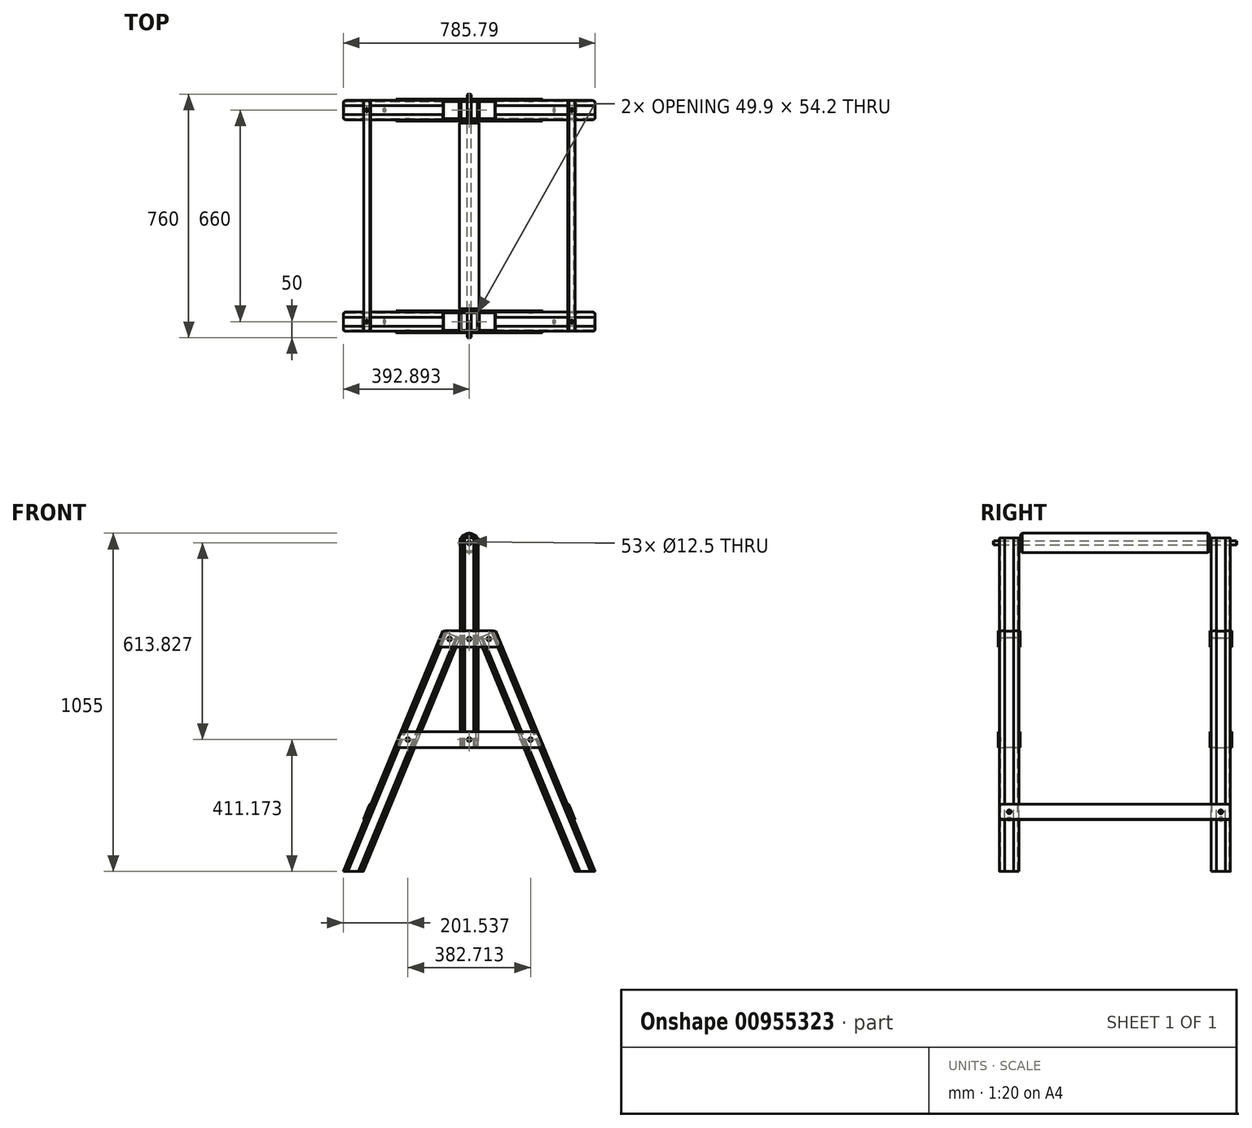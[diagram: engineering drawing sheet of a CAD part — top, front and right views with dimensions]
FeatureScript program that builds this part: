
annotation { "Feature Type Name" : "Feature", "Feature Type Description" : "" }
export const myFeature = defineFeature(function(context is Context, id is Id, definition is map)
    precondition{}
    {
        {
            var Q0;
            Q0=qCreatedBy(makeId("Front.planeOp"),FACE);
            var sketch = newSketch(context, id + "F0", { "sketchPlane" : qUnion([Q0])});
            skLineSegment(sketch, "E0", {"start": v(0, 0) * mm, "end": v(-310.74, 750.2) * mm});
            skLineSegment(sketch, "E1", {"start": v(-310.74, 750.2) * mm, "end": v(-364.05, 728.1) * mm});
            skLineSegment(sketch, "E2", {"start": v(-364.05, 728.1) * mm, "end": v(-62.45, 0) * mm});
            skLineSegment(sketch, "E3", {"start": v(-62.45, 0) * mm, "end": v(0, 0) * mm});
            skLineSegment(sketch, "E4", {"start": v(-337.4, 739.15) * mm, "end": v(-31.23, 0) * mm, "construction": true});
            skCircle(sketch, "E5", {"center": v(-331.65, 725.3) * mm, "radius": 6.25 * mm});
            skCircle(sketch, "E6", {"center": v(-201.54, 411.17) * mm, "radius": 6.25 * mm});
            skSolve(sketch);
        }
        {
            var Q0;
            Q0 = qSketchRegion(id + "F0", true);
            extrude(context, id + "F1", {"entities" : qUnion([Q0]), "depth" : 60 * mm, "offsetDistance" : 25 * mm});
        }
        {
            var Q0;
            Q0=makeQuery(id+"F1.opExtrude","CAP_EDGE",EDGE,{"disambiguationData":[OSD([sQuery(id+"F0.wireOp",EDGE,"E0")])],"isStart":false});
            var Q1;
            Q1=makeQuery(id+"F1.opExtrude","CAP_EDGE",EDGE,{"disambiguationData":[OSD([sQuery(id+"F0.wireOp",EDGE,"E2")])],"isStart":false});
            var Q2;
            Q2=makeQuery(id+"F1.opExtrude","CAP_EDGE",EDGE,{"disambiguationData":[OSD([sQuery(id+"F0.wireOp",EDGE,"E0")])],"isStart":true});
            var Q3;
            Q3=makeQuery(id+"F1.opExtrude","CAP_EDGE",EDGE,{"disambiguationData":[OSD([sQuery(id+"F0.wireOp",EDGE,"E2")])],"isStart":true});
            fillet(context, id + "F2", {"entities" : qUnion([Q0, Q1, Q2, Q3]), "radius" : 7.5 * mm, "tangentPropagation" : true, "allowEdgeOverflow" : false});
        }
        {
            var Q0;
            Q0=makeQuery(id+"F1.opExtrude","SWEPT_FACE",FACE,{"disambiguationData":[OSD([sQuery(id+"F0.wireOp",EDGE,"E1")])]});
            var sketch = newSketch(context, id + "F3", { "sketchPlane" : qUnion([Q0])});
            skLineSegment(sketch, "E7", {"start": v(-50.2, -60) * mm, "end": v(-49.2, -59) * mm});
            skLineSegment(sketch, "E8", {"start": v(-49.2, -59) * mm, "end": v(-48.2, -60) * mm});
            skLineSegment(sketch, "E9", {"start": v(-48.2, -60) * mm, "end": v(-47.2, -59) * mm});
            skLineSegment(sketch, "E10", {"start": v(-47.2, -59) * mm, "end": v(-46.2, -60) * mm});
            skLineSegment(sketch, "E11", {"start": v(-46.2, -60) * mm, "end": v(-45.2, -59) * mm});
            skLineSegment(sketch, "E12", {"start": v(-45.2, -59) * mm, "end": v(-44.2, -60) * mm});
            skLineSegment(sketch, "E13", {"start": v(-28.85, -60) * mm, "end": v(-28.85, -30) * mm, "construction": true});
            skPoint(sketch, "E13.endSnap0", {"position": v(-57.7, -30) * mm});
            skLineSegment(sketch, "E14", {"start": v(-28.85, -30) * mm, "end": v(-57.7, -30) * mm, "construction": true});
            skLineSegment(sketch, "E15", {"start": v(-57.4, -44) * mm, "end": v(-57.7, -44) * mm});
            skLineSegment(sketch, "E16", {"start": v(-57.4, -44) * mm, "end": v(-57.4, -30) * mm});
            skArc(sketch, "E17.0", {"start": v(-54.8, -52.5) * mm, "mid": v(-53.45, -55.75) * mm, "end": v(-50.2, -57.1) * mm});
            skLineSegment(sketch, "E18", {"start": v(-54.8, -52.5) * mm, "end": v(-54.8, -30) * mm});
            skLineSegment(sketch, "E19", {"start": v(-50.2, -57.1) * mm, "end": v(-28.85, -57.1) * mm});
            skLineSegment(sketch, "E20.MirrorCS", {"start": v(-0.3, -44) * mm, "end": v(0, -44) * mm});
            skLineSegment(sketch, "E21.MirrorCS", {"start": v(-7.5, -60) * mm, "end": v(-8.5, -59) * mm});
            skLineSegment(sketch, "E22.MirrorCS", {"start": v(-11.5, -60) * mm, "end": v(-12.5, -59) * mm});
            skLineSegment(sketch, "E23.MirrorCS", {"start": v(-9.5, -60) * mm, "end": v(-10.5, -59) * mm});
            skLineSegment(sketch, "E24.MirrorCS", {"start": v(-12.5, -59) * mm, "end": v(-13.5, -60) * mm});
            skLineSegment(sketch, "E25.MirrorCS", {"start": v(-10.5, -59) * mm, "end": v(-11.5, -60) * mm});
            skLineSegment(sketch, "E26.MirrorCS", {"start": v(-8.5, -59) * mm, "end": v(-9.5, -60) * mm});
            skArc(sketch, "E27.MirrorCS", {"start": v(-2.9, -52.5) * mm, "mid": v(-4.25, -55.75) * mm, "end": v(-7.5, -57.1) * mm});
            skLineSegment(sketch, "E28.MirrorCS", {"start": v(-0.3, -44) * mm, "end": v(-0.3, -30) * mm});
            skLineSegment(sketch, "E29.MirrorCS", {"start": v(-7.5, -57.1) * mm, "end": v(-28.85, -57.1) * mm});
            skLineSegment(sketch, "E30.MirrorCS", {"start": v(-2.9, -52.5) * mm, "end": v(-2.9, -30) * mm});
            skLineSegment(sketch, "E31.MirrorCS", {"start": v(-50.2, 0) * mm, "end": v(-49.2, -1) * mm});
            skLineSegment(sketch, "E32.MirrorCS", {"start": v(-48.2, 0) * mm, "end": v(-47.2, -1) * mm});
            skLineSegment(sketch, "E33.MirrorCS", {"start": v(-49.2, -1) * mm, "end": v(-48.2, 0) * mm});
            skLineSegment(sketch, "E34.MirrorCS", {"start": v(-46.2, 0) * mm, "end": v(-45.2, -1) * mm});
            skLineSegment(sketch, "E35.MirrorCS", {"start": v(-47.2, -1) * mm, "end": v(-46.2, 0) * mm});
            skLineSegment(sketch, "E36.MirrorCS", {"start": v(-57.4, -16) * mm, "end": v(-57.7, -16) * mm});
            skLineSegment(sketch, "E37.MirrorCS", {"start": v(-45.2, -1) * mm, "end": v(-44.2, 0) * mm});
            skArc(sketch, "E38.MirrorCS", {"start": v(-54.8, -7.5) * mm, "mid": v(-53.45, -4.25) * mm, "end": v(-50.2, -2.9) * mm});
            skLineSegment(sketch, "E39.MirrorCS", {"start": v(-50.2, -2.9) * mm, "end": v(-28.85, -2.9) * mm});
            skLineSegment(sketch, "E40.MirrorCS", {"start": v(-54.8, -7.5) * mm, "end": v(-54.8, -30) * mm});
            skLineSegment(sketch, "E41.MirrorCS", {"start": v(-57.4, -16) * mm, "end": v(-57.4, -30) * mm});
            skLineSegment(sketch, "E42.MirrorCS", {"start": v(-9.5, 0) * mm, "end": v(-10.5, -1) * mm});
            skLineSegment(sketch, "E43.MirrorCS", {"start": v(-12.5, -1) * mm, "end": v(-13.5, 0) * mm});
            skLineSegment(sketch, "E44.MirrorCS", {"start": v(-10.5, -1) * mm, "end": v(-11.5, 0) * mm});
            skLineSegment(sketch, "E45.MirrorCS", {"start": v(-0.3, -16) * mm, "end": v(0, -16) * mm});
            skLineSegment(sketch, "E46.MirrorCS", {"start": v(-11.5, 0) * mm, "end": v(-12.5, -1) * mm});
            skLineSegment(sketch, "E47.MirrorCS", {"start": v(-7.5, 0) * mm, "end": v(-8.5, -1) * mm});
            skLineSegment(sketch, "E48.MirrorCS", {"start": v(-8.5, -1) * mm, "end": v(-9.5, 0) * mm});
            skLineSegment(sketch, "E49.MirrorCS", {"start": v(-2.9, -7.5) * mm, "end": v(-2.9, -30) * mm});
            skLineSegment(sketch, "E50.MirrorCS", {"start": v(-7.5, -2.9) * mm, "end": v(-28.85, -2.9) * mm});
            skArc(sketch, "E51.MirrorCS", {"start": v(-2.9, -7.5) * mm, "mid": v(-4.25, -4.25) * mm, "end": v(-7.5, -2.9) * mm});
            skLineSegment(sketch, "E52.MirrorCS", {"start": v(-0.3, -16) * mm, "end": v(-0.3, -30) * mm});
            skSolve(sketch);
        }
        {
            var Q0;
            Q0=makeQuery(id+"F3.imprint","IMPRINT",FACE,{"disambiguationData":[TD([[makeQuery(id+"F3.imprint","IMPRINT",EDGE,{"derivedFrom":sQuery(id+"F3.wireOp",EDGE,"E17.0")}),1.0]])]});
            var Q1;
            {var subQ0=sQuery(id+"F3.wireOp",EDGE,"E34.MirrorCS");Q1=makeQuery(id+"F3.imprint","IMPRINT",FACE,{"disambiguationData":[TD([[makeQuery(id+"F3.imprint","IMPRINT",EDGE,{"derivedFrom":subQ0}),1.0]])]});}
            var Q2;
            {var subQ0=sQuery(id+"F3.wireOp",EDGE,"E32.MirrorCS");Q2=makeQuery(id+"F3.imprint","IMPRINT",FACE,{"disambiguationData":[TD([[makeQuery(id+"F3.imprint","IMPRINT",EDGE,{"derivedFrom":subQ0}),1.0]])]});}
            var Q3;
            {var subQ0=sQuery(id+"F3.wireOp",EDGE,"E31.MirrorCS");Q3=makeQuery(id+"F3.imprint","IMPRINT",FACE,{"disambiguationData":[TD([[makeQuery(id+"F3.imprint","IMPRINT",EDGE,{"derivedFrom":subQ0}),1.0]])]});}
            var Q4;
            {var subQ1=sQuery(id+"F3.wireOp",EDGE,"E15");Q4=makeQuery(id+"F3.imprint","IMPRINT",FACE,{"disambiguationData":[TD([[makeQuery(id+"F3.imprint","IMPRINT",EDGE,{"derivedFrom":subQ1}),-1.0]])]});}
            var Q5;
            {var subQ0=sQuery(id+"F3.wireOp",EDGE,"E7");Q5=makeQuery(id+"F3.imprint","IMPRINT",FACE,{"disambiguationData":[TD([[makeQuery(id+"F3.imprint","IMPRINT",EDGE,{"derivedFrom":subQ0}),-1.0]])]});}
            var Q6;
            {var subQ0=sQuery(id+"F3.wireOp",EDGE,"E9");Q6=makeQuery(id+"F3.imprint","IMPRINT",FACE,{"disambiguationData":[TD([[makeQuery(id+"F3.imprint","IMPRINT",EDGE,{"derivedFrom":subQ0}),-1.0]])]});}
            var Q7;
            {var subQ0=sQuery(id+"F3.wireOp",EDGE,"E11");Q7=makeQuery(id+"F3.imprint","IMPRINT",FACE,{"disambiguationData":[TD([[makeQuery(id+"F3.imprint","IMPRINT",EDGE,{"derivedFrom":subQ0}),-1.0]])]});}
            var Q8;
            {var subQ0=sQuery(id+"F3.wireOp",EDGE,"E21.MirrorCS");Q8=makeQuery(id+"F3.imprint","IMPRINT",FACE,{"disambiguationData":[TD([[makeQuery(id+"F3.imprint","IMPRINT",EDGE,{"derivedFrom":subQ0}),1.0]])]});}
            var Q9;
            {var subQ0=sQuery(id+"F3.wireOp",EDGE,"E23.MirrorCS");Q9=makeQuery(id+"F3.imprint","IMPRINT",FACE,{"disambiguationData":[TD([[makeQuery(id+"F3.imprint","IMPRINT",EDGE,{"derivedFrom":subQ0}),1.0]])]});}
            var Q10;
            {var subQ0=sQuery(id+"F3.wireOp",EDGE,"E22.MirrorCS");Q10=makeQuery(id+"F3.imprint","IMPRINT",FACE,{"disambiguationData":[TD([[makeQuery(id+"F3.imprint","IMPRINT",EDGE,{"derivedFrom":subQ0}),1.0]])]});}
            var Q11;
            {var subQ1=sQuery(id+"F3.wireOp",EDGE,"E20.MirrorCS");Q11=makeQuery(id+"F3.imprint","IMPRINT",FACE,{"disambiguationData":[TD([[makeQuery(id+"F3.imprint","IMPRINT",EDGE,{"derivedFrom":subQ1}),1.0]])]});}
            var Q12;
            {var subQ0=sQuery(id+"F3.wireOp",EDGE,"E47.MirrorCS");Q12=makeQuery(id+"F3.imprint","IMPRINT",FACE,{"disambiguationData":[TD([[makeQuery(id+"F3.imprint","IMPRINT",EDGE,{"derivedFrom":subQ0}),-1.0]])]});}
            var Q13;
            {var subQ0=sQuery(id+"F3.wireOp",EDGE,"E42.MirrorCS");Q13=makeQuery(id+"F3.imprint","IMPRINT",FACE,{"disambiguationData":[TD([[makeQuery(id+"F3.imprint","IMPRINT",EDGE,{"derivedFrom":subQ0}),-1.0]])]});}
            var Q14;
            {var subQ0=sQuery(id+"F3.wireOp",EDGE,"E43.MirrorCS");Q14=makeQuery(id+"F3.imprint","IMPRINT",FACE,{"disambiguationData":[TD([[makeQuery(id+"F3.imprint","IMPRINT",EDGE,{"derivedFrom":subQ0}),-1.0]])]});}
            var Q15;
            Q15=makeQuery(id+"F1.opExtrude","SWEPT_FACE",FACE,{"disambiguationData":[OSD([sQuery(id+"F0.wireOp",EDGE,"E3")])]});
            extrude(context, id + "F4", {"entities" : qUnion([Q0, Q1, Q2, Q3, Q4, Q5, Q6, Q7, Q8, Q9, Q10, Q11, Q12, Q13, Q14]), "operationType" : NewBodyOperationType.REMOVE, "endBound" : BoundingType.UP_TO_SURFACE, "oppositeDirection" : true, "depth" : 25 * mm, "endBoundEntityFace" : qUnion([Q15]), "offsetDistance" : 25 * mm});
        }
        {
            var Q0;
            {var subQ0=sQuery(id+"F0.wireOp",EDGE,"E0");Q0=makeQuery(id+"F4.boolean.opBoolean","SPLIT",FACE,{"disambiguationData":[TD([makeQuery(id+"F4.opExtrude","SWEPT_FACE",FACE,{"disambiguationData":[OSD([sQuery(id+"F3.wireOp",EDGE,"E20.MirrorCS")])]})])],"derivedFrom":makeQuery(id+"F1.opExtrude","SWEPT_FACE",FACE,{"disambiguationData":[OSD([subQ0])]})});}
            var sketch = newSketch(context, id + "F5", { "sketchPlane" : qUnion([Q0])});
            skLineSegment(sketch, "E53", {"start": v(-60, 0) * mm, "end": v(0, 0) * mm, "construction": true});
            skLineSegment(sketch, "E54", {"start": v(-30, 0) * mm, "end": v(-30, 812) * mm, "construction": true});
            skCircle(sketch, "E55", {"center": v(-30, 200) * mm, "radius": 6.25 * mm});
            skSolve(sketch);
        }
        {
            var Q0;
            Q0 = qSketchRegion(id + "F5", true);
            var Q1;
            {var subQ0=sQuery(id+"F0.wireOp",EDGE,"E2");Q1=makeQuery(id+"F4.boolean.opBoolean","SPLIT",FACE,{"disambiguationData":[TD([makeQuery(id+"F4.opExtrude","SWEPT_FACE",FACE,{"disambiguationData":[OSD([sQuery(id+"F3.wireOp",EDGE,"E15")])]})])],"derivedFrom":makeQuery(id+"F1.opExtrude","SWEPT_FACE",FACE,{"disambiguationData":[OSD([subQ0])]})});}
            extrude(context, id + "F6", {"entities" : qUnion([Q0]), "operationType" : NewBodyOperationType.REMOVE, "endBound" : BoundingType.UP_TO_SURFACE, "oppositeDirection" : true, "depth" : 25 * mm, "endBoundEntityFace" : qUnion([Q1]), "offsetDistance" : 25 * mm});
        }
        {
            var Q0;
            Q0=makeQuery(id+"F1.opExtrude","CAP_FACE",FACE,{"disambiguationData":[OSD([sQuery(id+"F0.wireOp",EDGE,"E0"),sQuery(id+"F0.wireOp",EDGE,"E1"),sQuery(id+"F0.wireOp",EDGE,"E2"),sQuery(id+"F0.wireOp",EDGE,"E3")])],"isStart":false});
            var sketch = newSketch(context, id + "F7", { "sketchPlane" : qUnion([Q0])});
            skLineSegment(sketch, "E56", {"start": v(-365.05, 1040) * mm, "end": v(-365.05, 386.17) * mm});
            skLineSegment(sketch, "E57", {"start": v(-365.05, 386.17) * mm, "end": v(-420.75, 386.17) * mm});
            skLineSegment(sketch, "E58", {"start": v(-420.75, 386.17) * mm, "end": v(-420.75, 1040) * mm});
            skLineSegment(sketch, "E59", {"start": v(-420.75, 1040) * mm, "end": v(-365.05, 1040) * mm});
            skLineSegment(sketch, "E60", {"start": v(-392.9, 386.17) * mm, "end": v(-392.9, 1040) * mm, "construction": true});
            skCircle(sketch, "E61", {"center": v(-392.9, 725.3) * mm, "radius": 6.25 * mm});
            skLineSegment(sketch, "E62", {"start": v(-420.75, 719.04) * mm, "end": v(-297.84, 719.04) * mm, "construction": true});
            skLineSegment(sketch, "E63", {"start": v(-420.75, 404.92) * mm, "end": v(-167.72, 404.92) * mm, "construction": true});
            skCircle(sketch, "E64", {"center": v(-392.9, 411.17) * mm, "radius": 6.25 * mm});
            skCircle(sketch, "E65", {"center": v(-392.9, 1025) * mm, "radius": 6.25 * mm});
            skSolve(sketch);
        }
        {
            var Q0;
            Q0 = qSketchRegion(id + "F7", true);
            extrude(context, id + "F8", {"entities" : qUnion([Q0]), "oppositeDirection" : true, "depth" : 60 * mm, "offsetDistance" : 25 * mm});
        }
        {
            var Q0;
            Q0=makeQuery(id+"F8.opExtrude","CAP_EDGE",EDGE,{"disambiguationData":[OSD([sQuery(id+"F7.wireOp",EDGE,"E58")])],"isStart":true});
            var Q1;
            Q1=makeQuery(id+"F8.opExtrude","CAP_EDGE",EDGE,{"disambiguationData":[OSD([sQuery(id+"F7.wireOp",EDGE,"E56")])],"isStart":true});
            var Q2;
            Q2=makeQuery(id+"F8.opExtrude","CAP_EDGE",EDGE,{"disambiguationData":[OSD([sQuery(id+"F7.wireOp",EDGE,"E56")])],"isStart":false});
            var Q3;
            Q3=makeQuery(id+"F8.opExtrude","CAP_EDGE",EDGE,{"disambiguationData":[OSD([sQuery(id+"F7.wireOp",EDGE,"E58")])],"isStart":false});
            fillet(context, id + "F9", {"entities" : qUnion([Q0, Q1, Q2, Q3]), "radius" : 7.5 * mm, "tangentPropagation" : true, "allowEdgeOverflow" : false});
        }
        {
            var Q0;
            Q0=makeQuery(id+"F8.opExtrude","SWEPT_FACE",FACE,{"disambiguationData":[OSD([sQuery(id+"F7.wireOp",EDGE,"E59")])]});
            var sketch = newSketch(context, id + "F10", { "sketchPlane" : qUnion([Q0])});
            skLineSegment(sketch, "E66", {"start": v(-420.75, -30) * mm, "end": v(-392.9, -30) * mm, "construction": true});
            skPoint(sketch, "E66.endSnap0", {"position": v(-392.9, -60) * mm});
            skLineSegment(sketch, "E67", {"start": v(-392.9, -30) * mm, "end": v(-392.9, -60) * mm, "construction": true});
            skLineSegment(sketch, "E68", {"start": v(-413.25, -60) * mm, "end": v(-412.25, -59) * mm});
            skLineSegment(sketch, "E69", {"start": v(-412.25, -59) * mm, "end": v(-411.25, -60) * mm});
            skLineSegment(sketch, "E70", {"start": v(-420.45, -30) * mm, "end": v(-420.45, -44) * mm});
            skLineSegment(sketch, "E71", {"start": v(-420.45, -44) * mm, "end": v(-420.75, -44) * mm});
            skLineSegment(sketch, "E72", {"start": v(-411.25, -60) * mm, "end": v(-410.25, -59) * mm});
            skLineSegment(sketch, "E73", {"start": v(-410.25, -59) * mm, "end": v(-409.25, -60) * mm});
            skLineSegment(sketch, "E74", {"start": v(-409.25, -60) * mm, "end": v(-408.25, -59) * mm});
            skLineSegment(sketch, "E75", {"start": v(-408.25, -59) * mm, "end": v(-407.25, -60) * mm});
            skArc(sketch, "E76.0", {"start": v(-417.85, -52.5) * mm, "mid": v(-416.5, -55.75) * mm, "end": v(-413.25, -57.1) * mm});
            skLineSegment(sketch, "E77", {"start": v(-417.85, -52.5) * mm, "end": v(-417.85, -30) * mm});
            skLineSegment(sketch, "E78", {"start": v(-413.25, -57.1) * mm, "end": v(-392.9, -57.1) * mm});
            skLineSegment(sketch, "E79.MirrorCS", {"start": v(-365.35, -44) * mm, "end": v(-365.05, -44) * mm});
            skLineSegment(sketch, "E80.MirrorCS", {"start": v(-372.55, -60) * mm, "end": v(-373.55, -59) * mm});
            skLineSegment(sketch, "E81.MirrorCS", {"start": v(-373.55, -59) * mm, "end": v(-374.55, -60) * mm});
            skLineSegment(sketch, "E82.MirrorCS", {"start": v(-377.55, -59) * mm, "end": v(-378.55, -60) * mm});
            skLineSegment(sketch, "E83.MirrorCS", {"start": v(-374.55, -60) * mm, "end": v(-375.55, -59) * mm});
            skLineSegment(sketch, "E84.MirrorCS", {"start": v(-375.55, -59) * mm, "end": v(-376.55, -60) * mm});
            skLineSegment(sketch, "E85.MirrorCS", {"start": v(-376.55, -60) * mm, "end": v(-377.55, -59) * mm});
            skArc(sketch, "E86.MirrorCS", {"start": v(-367.95, -52.5) * mm, "mid": v(-369.3, -55.75) * mm, "end": v(-372.55, -57.1) * mm});
            skLineSegment(sketch, "E87.MirrorCS", {"start": v(-365.35, -30) * mm, "end": v(-365.35, -44) * mm});
            skLineSegment(sketch, "E88.MirrorCS", {"start": v(-372.55, -57.1) * mm, "end": v(-392.9, -57.1) * mm});
            skLineSegment(sketch, "E89.MirrorCS", {"start": v(-367.95, -52.5) * mm, "end": v(-367.95, -30) * mm});
            skLineSegment(sketch, "E90.MirrorCS", {"start": v(-411.25, 0) * mm, "end": v(-410.25, -1) * mm});
            skLineSegment(sketch, "E91.MirrorCS", {"start": v(-413.25, 0) * mm, "end": v(-412.25, -1) * mm});
            skLineSegment(sketch, "E92.MirrorCS", {"start": v(-412.25, -1) * mm, "end": v(-411.25, 0) * mm});
            skLineSegment(sketch, "E93.MirrorCS", {"start": v(-410.25, -1) * mm, "end": v(-409.25, 0) * mm});
            skLineSegment(sketch, "E94.MirrorCS", {"start": v(-420.45, -16) * mm, "end": v(-420.75, -16) * mm});
            skLineSegment(sketch, "E95.MirrorCS", {"start": v(-409.25, 0) * mm, "end": v(-408.25, -1) * mm});
            skLineSegment(sketch, "E96.MirrorCS", {"start": v(-408.25, -1) * mm, "end": v(-407.25, 0) * mm});
            skArc(sketch, "E97.MirrorCS", {"start": v(-417.85, -7.5) * mm, "mid": v(-416.5, -4.25) * mm, "end": v(-413.25, -2.9) * mm});
            skLineSegment(sketch, "E98.MirrorCS", {"start": v(-413.25, -2.9) * mm, "end": v(-392.9, -2.9) * mm});
            skLineSegment(sketch, "E99.MirrorCS", {"start": v(-417.85, -7.5) * mm, "end": v(-417.85, -30) * mm});
            skLineSegment(sketch, "E100.MirrorCS", {"start": v(-420.45, -30) * mm, "end": v(-420.45, -16) * mm});
            skLineSegment(sketch, "E101.MirrorCS", {"start": v(-375.55, -1) * mm, "end": v(-376.55, 0) * mm});
            skLineSegment(sketch, "E102.MirrorCS", {"start": v(-376.55, 0) * mm, "end": v(-377.55, -1) * mm});
            skLineSegment(sketch, "E103.MirrorCS", {"start": v(-372.55, 0) * mm, "end": v(-373.55, -1) * mm});
            skLineSegment(sketch, "E104.MirrorCS", {"start": v(-373.55, -1) * mm, "end": v(-374.55, 0) * mm});
            skLineSegment(sketch, "E105.MirrorCS", {"start": v(-374.55, 0) * mm, "end": v(-375.55, -1) * mm});
            skLineSegment(sketch, "E106.MirrorCS", {"start": v(-365.35, -16) * mm, "end": v(-365.05, -16) * mm});
            skLineSegment(sketch, "E107.MirrorCS", {"start": v(-377.55, -1) * mm, "end": v(-378.55, 0) * mm});
            skArc(sketch, "E108.MirrorCS", {"start": v(-367.95, -7.5) * mm, "mid": v(-369.3, -4.25) * mm, "end": v(-372.55, -2.9) * mm});
            skLineSegment(sketch, "E109.MirrorCS", {"start": v(-365.35, -30) * mm, "end": v(-365.35, -16) * mm});
            skLineSegment(sketch, "E110.MirrorCS", {"start": v(-367.95, -7.5) * mm, "end": v(-367.95, -30) * mm});
            skLineSegment(sketch, "E111.MirrorCS", {"start": v(-372.55, -2.9) * mm, "end": v(-392.9, -2.9) * mm});
            skSolve(sketch);
        }
        {
            var Q0;
            {var subQ0=sQuery(id+"F10.wireOp",EDGE,"E68");Q0=makeQuery(id+"F10.imprint","IMPRINT",FACE,{"disambiguationData":[TD([[makeQuery(id+"F10.imprint","IMPRINT",EDGE,{"derivedFrom":subQ0}),-1.0]])]});}
            var Q1;
            {var subQ0=sQuery(id+"F10.wireOp",EDGE,"E72");Q1=makeQuery(id+"F10.imprint","IMPRINT",FACE,{"disambiguationData":[TD([[makeQuery(id+"F10.imprint","IMPRINT",EDGE,{"derivedFrom":subQ0}),-1.0]])]});}
            var Q2;
            {var subQ0=sQuery(id+"F10.wireOp",EDGE,"E74");Q2=makeQuery(id+"F10.imprint","IMPRINT",FACE,{"disambiguationData":[TD([[makeQuery(id+"F10.imprint","IMPRINT",EDGE,{"derivedFrom":subQ0}),-1.0]])]});}
            var Q3;
            {var subQ0=sQuery(id+"F10.wireOp",EDGE,"E82.MirrorCS");Q3=makeQuery(id+"F10.imprint","IMPRINT",FACE,{"disambiguationData":[TD([[makeQuery(id+"F10.imprint","IMPRINT",EDGE,{"derivedFrom":subQ0}),1.0]])]});}
            var Q4;
            {var subQ0=sQuery(id+"F10.wireOp",EDGE,"E83.MirrorCS");Q4=makeQuery(id+"F10.imprint","IMPRINT",FACE,{"disambiguationData":[TD([[makeQuery(id+"F10.imprint","IMPRINT",EDGE,{"derivedFrom":subQ0}),1.0]])]});}
            var Q5;
            {var subQ0=sQuery(id+"F10.wireOp",EDGE,"E80.MirrorCS");Q5=makeQuery(id+"F10.imprint","IMPRINT",FACE,{"disambiguationData":[TD([[makeQuery(id+"F10.imprint","IMPRINT",EDGE,{"derivedFrom":subQ0}),1.0]])]});}
            var Q6;
            Q6=makeQuery(id+"F10.imprint","IMPRINT",FACE,{"disambiguationData":[TD([[makeQuery(id+"F10.imprint","IMPRINT",EDGE,{"derivedFrom":sQuery(id+"F10.wireOp",EDGE,"E70")}),-1.0]])]});
            var Q7;
            {var subQ1=sQuery(id+"F10.wireOp",EDGE,"E79.MirrorCS");Q7=makeQuery(id+"F10.imprint","IMPRINT",FACE,{"disambiguationData":[TD([[makeQuery(id+"F10.imprint","IMPRINT",EDGE,{"derivedFrom":subQ1}),1.0]])]});}
            var Q8;
            {var subQ0=sQuery(id+"F10.wireOp",EDGE,"E102.MirrorCS");Q8=makeQuery(id+"F10.imprint","IMPRINT",FACE,{"disambiguationData":[TD([[makeQuery(id+"F10.imprint","IMPRINT",EDGE,{"derivedFrom":subQ0}),-1.0]])]});}
            var Q9;
            {var subQ0=sQuery(id+"F10.wireOp",EDGE,"E101.MirrorCS");Q9=makeQuery(id+"F10.imprint","IMPRINT",FACE,{"disambiguationData":[TD([[makeQuery(id+"F10.imprint","IMPRINT",EDGE,{"derivedFrom":subQ0}),-1.0]])]});}
            var Q10;
            {var subQ0=sQuery(id+"F10.wireOp",EDGE,"E103.MirrorCS");Q10=makeQuery(id+"F10.imprint","IMPRINT",FACE,{"disambiguationData":[TD([[makeQuery(id+"F10.imprint","IMPRINT",EDGE,{"derivedFrom":subQ0}),-1.0]])]});}
            var Q11;
            {var subQ0=sQuery(id+"F10.wireOp",EDGE,"E91.MirrorCS");Q11=makeQuery(id+"F10.imprint","IMPRINT",FACE,{"disambiguationData":[TD([[makeQuery(id+"F10.imprint","IMPRINT",EDGE,{"derivedFrom":subQ0}),1.0]])]});}
            var Q12;
            {var subQ0=sQuery(id+"F10.wireOp",EDGE,"E90.MirrorCS");Q12=makeQuery(id+"F10.imprint","IMPRINT",FACE,{"disambiguationData":[TD([[makeQuery(id+"F10.imprint","IMPRINT",EDGE,{"derivedFrom":subQ0}),1.0]])]});}
            var Q13;
            {var subQ0=sQuery(id+"F10.wireOp",EDGE,"E95.MirrorCS");Q13=makeQuery(id+"F10.imprint","IMPRINT",FACE,{"disambiguationData":[TD([[makeQuery(id+"F10.imprint","IMPRINT",EDGE,{"derivedFrom":subQ0}),1.0]])]});}
            var Q14;
            Q14=makeQuery(id+"F10.imprint","IMPRINT",FACE,{"disambiguationData":[TD([[makeQuery(id+"F10.imprint","IMPRINT",EDGE,{"derivedFrom":sQuery(id+"F10.wireOp",EDGE,"E76.0")}),1.0]])]});
            var Q15;
            Q15=makeQuery(id+"F8.opExtrude","SWEPT_FACE",FACE,{"disambiguationData":[OSD([sQuery(id+"F7.wireOp",EDGE,"E57")])]});
            extrude(context, id + "F11", {"entities" : qUnion([Q0, Q1, Q2, Q3, Q4, Q5, Q6, Q7, Q8, Q9, Q10, Q11, Q12, Q13, Q14]), "operationType" : NewBodyOperationType.REMOVE, "endBound" : BoundingType.UP_TO_SURFACE, "oppositeDirection" : true, "depth" : 25 * mm, "endBoundEntityFace" : qUnion([Q15]), "offsetDistance" : 25 * mm});
        }
        {
            var Q0;
            Q0=makeQuery(id+"F11.boolean.opBoolean","COPY",FACE,{"derivedFrom":makeQuery(id+"F11.opExtrude","SWEPT_FACE",FACE,{"disambiguationData":[OSD([sQuery(id+"F10.wireOp",EDGE,"E87.MirrorCS"),sQuery(id+"F10.wireOp",EDGE,"E109.MirrorCS")])]})});
            var Q1;
            Q1=makeQuery(id+"F11.boolean.opBoolean","COPY",FACE,{"derivedFrom":makeQuery(id+"F11.opExtrude","SWEPT_FACE",FACE,{"disambiguationData":[OSD([sQuery(id+"F10.wireOp",EDGE,"E70"),sQuery(id+"F10.wireOp",EDGE,"E100.MirrorCS")])]})});
            cPlane(context, id + "F12", {"entities" : qUnion([Q0, Q1]), "cplaneType" : CPlaneType.MID_PLANE, "offset" : 25 * mm, "width" : 150 * mm, "height" : 150 * mm});
        }
        {
            var Q0;
            Q0=makeQuery(id+"F1.opExtrude","SWEPT_BODY",BODY,{"disambiguationData":[OSD([sQuery(id+"F0.wireOp",EDGE,"E0"),sQuery(id+"F0.wireOp",EDGE,"E1"),sQuery(id+"F0.wireOp",EDGE,"E2"),sQuery(id+"F0.wireOp",EDGE,"E3")])]});
            var Q1;
            Q1=qCreatedBy(id+"F12.planeOp",FACE);
            mirror(context, id + "F13", {"entities" : qUnion([Q0]), "mirrorPlane" : qUnion([Q1])});
        }
        {
            var Q0;
            Q0=makeQuery(id+"F13.opPattern","COPY",FACE,{"derivedFrom":makeQuery(id+"F1.opExtrude","CAP_FACE",FACE,{"disambiguationData":[OSD([sQuery(id+"F0.wireOp",EDGE,"E0"),sQuery(id+"F0.wireOp",EDGE,"E1"),sQuery(id+"F0.wireOp",EDGE,"E2"),sQuery(id+"F0.wireOp",EDGE,"E3")])],"isStart":false}),"instanceName":"1"});
            var sketch = newSketch(context, id + "F14", { "sketchPlane" : qUnion([Q0])});
            skLineSegment(sketch, "E112", {"start": v(-605.13, 436.17) * mm, "end": v(-625.84, 386.17) * mm});
            skLineSegment(sketch, "E113", {"start": v(-625.84, 386.17) * mm, "end": v(-159.96, 386.17) * mm});
            skLineSegment(sketch, "E114", {"start": v(-159.96, 386.17) * mm, "end": v(-180.67, 436.17) * mm});
            skLineSegment(sketch, "E115", {"start": v(-180.67, 436.17) * mm, "end": v(-605.13, 436.17) * mm});
            skLineSegment(sketch, "E116", {"start": v(-475.05, 750.2) * mm, "end": v(-495.77, 700.2) * mm});
            skLineSegment(sketch, "E117", {"start": v(-495.77, 700.2) * mm, "end": v(-290.03, 700.2) * mm});
            skLineSegment(sketch, "E118", {"start": v(-290.03, 700.2) * mm, "end": v(-310.74, 750.2) * mm});
            skLineSegment(sketch, "E119", {"start": v(-310.74, 750.2) * mm, "end": v(-475.05, 750.2) * mm});
            skLineSegment(sketch, "E120", {"start": v(-392.9, 750.2) * mm, "end": v(-392.9, 700.2) * mm, "construction": true});
            skLineSegment(sketch, "E121", {"start": v(-485.4, 725.2) * mm, "end": v(-300.38, 725.2) * mm, "construction": true});
            skLineSegment(sketch, "E122", {"start": v(-615.48, 411.17) * mm, "end": v(-170.31, 411.17) * mm, "construction": true});
            skLineSegment(sketch, "E123", {"start": v(-392.9, 436.17) * mm, "end": v(-392.9, 386.17) * mm, "construction": true});
            skCircle(sketch, "E124", {"center": v(-392.9, 411.17) * mm, "radius": 6.25 * mm});
            skCircle(sketch, "E125", {"center": v(-392.9, 725.2) * mm, "radius": 6.25 * mm});
            skCircle(sketch, "E126", {"center": v(-454.14, 725.3) * mm, "radius": 6.25 * mm});
            skCircle(sketch, "E127", {"center": v(-331.65, 725.3) * mm, "radius": 6.25 * mm});
            skCircle(sketch, "E128", {"center": v(-201.54, 411.17) * mm, "radius": 6.25 * mm});
            skCircle(sketch, "E129", {"center": v(-584.25, 411.17) * mm, "radius": 6.25 * mm});
            skSolve(sketch);
        }
        {
            var Q0;
            Q0 = qSketchRegion(id + "F14", true);
            extrude(context, id + "F15", {"entities" : qUnion([Q0]), "depth" : 4 * mm, "offsetDistance" : 25 * mm});
        }
        {
            var Q0;
            Q0=makeQuery(id+"F15.opExtrude","SWEPT_EDGE",EDGE,{"disambiguationData":[OSD([sQuery(id+"F14.wireOp",EDGE,"E116"),sQuery(id+"F14.wireOp",EDGE,"E119")])]});
            var Q1;
            Q1=makeQuery(id+"F15.opExtrude","SWEPT_EDGE",EDGE,{"disambiguationData":[OSD([sQuery(id+"F14.wireOp",EDGE,"E116"),sQuery(id+"F14.wireOp",EDGE,"E117")])]});
            var Q2;
            Q2=makeQuery(id+"F15.opExtrude","SWEPT_EDGE",EDGE,{"disambiguationData":[OSD([sQuery(id+"F14.wireOp",EDGE,"E118"),sQuery(id+"F14.wireOp",EDGE,"E119")])]});
            var Q3;
            Q3=makeQuery(id+"F15.opExtrude","SWEPT_EDGE",EDGE,{"disambiguationData":[OSD([sQuery(id+"F14.wireOp",EDGE,"E117"),sQuery(id+"F14.wireOp",EDGE,"E118")])]});
            var Q4;
            Q4=makeQuery(id+"F15.opExtrude","SWEPT_EDGE",EDGE,{"disambiguationData":[OSD([sQuery(id+"F14.wireOp",EDGE,"E112"),sQuery(id+"F14.wireOp",EDGE,"E113")])]});
            var Q5;
            Q5=makeQuery(id+"F15.opExtrude","SWEPT_EDGE",EDGE,{"disambiguationData":[OSD([sQuery(id+"F14.wireOp",EDGE,"E112"),sQuery(id+"F14.wireOp",EDGE,"E115")])]});
            var Q6;
            Q6=makeQuery(id+"F15.opExtrude","SWEPT_EDGE",EDGE,{"disambiguationData":[OSD([sQuery(id+"F14.wireOp",EDGE,"E114"),sQuery(id+"F14.wireOp",EDGE,"E115")])]});
            var Q7;
            Q7=makeQuery(id+"F15.opExtrude","SWEPT_EDGE",EDGE,{"disambiguationData":[OSD([sQuery(id+"F14.wireOp",EDGE,"E113"),sQuery(id+"F14.wireOp",EDGE,"E114")])]});
            fillet(context, id + "F16", {"entities" : qUnion([Q0, Q1, Q2, Q3, Q4, Q5, Q6, Q7]), "radius" : 10 * mm, "tangentPropagation" : true, "allowEdgeOverflow" : false});
        }
        {
            var Q0;
            Q0=makeQuery(id+"F11.boolean.opBoolean","COPY",FACE,{"derivedFrom":makeQuery(id+"F11.opExtrude","SWEPT_FACE",FACE,{"disambiguationData":[OSD([sQuery(id+"F10.wireOp",EDGE,"E98.MirrorCS"),sQuery(id+"F10.wireOp",EDGE,"E111.MirrorCS")])]})});
            var Q1;
            Q1=makeQuery(id+"F11.boolean.opBoolean","COPY",FACE,{"derivedFrom":makeQuery(id+"F11.opExtrude","SWEPT_FACE",FACE,{"disambiguationData":[OSD([sQuery(id+"F10.wireOp",EDGE,"E78"),sQuery(id+"F10.wireOp",EDGE,"E88.MirrorCS")])]})});
            cPlane(context, id + "F17", {"entities" : qUnion([Q0, Q1]), "cplaneType" : CPlaneType.MID_PLANE, "offset" : 25 * mm, "width" : 150 * mm, "height" : 150 * mm});
        }
        {
            var Q0;
            Q0=makeQuery(id+"F15.opExtrude","SWEPT_BODY",BODY,{"disambiguationData":[OSD([sQuery(id+"F14.wireOp",EDGE,"E112"),sQuery(id+"F14.wireOp",EDGE,"E113"),sQuery(id+"F14.wireOp",EDGE,"E114"),sQuery(id+"F14.wireOp",EDGE,"E115"),sQuery(id+"F14.wireOp",EDGE,"E124"),sQuery(id+"F14.wireOp",EDGE,"E128"),sQuery(id+"F14.wireOp",EDGE,"E129")])]});
            var Q1;
            Q1=makeQuery(id+"F15.opExtrude","SWEPT_BODY",BODY,{"disambiguationData":[OSD([sQuery(id+"F14.wireOp",EDGE,"E116"),sQuery(id+"F14.wireOp",EDGE,"E117"),sQuery(id+"F14.wireOp",EDGE,"E118"),sQuery(id+"F14.wireOp",EDGE,"E119"),sQuery(id+"F14.wireOp",EDGE,"E125"),sQuery(id+"F14.wireOp",EDGE,"E126"),sQuery(id+"F14.wireOp",EDGE,"E127")])]});
            var Q2;
            Q2=qCreatedBy(id+"F17.planeOp",FACE);
            mirror(context, id + "F18", {"entities" : qUnion([Q0, Q1]), "mirrorPlane" : qUnion([Q2])});
        }
        {
            var Q0;
            Q0=makeQuery(id+"F8.opExtrude","CAP_FACE",FACE,{"disambiguationData":[OSD([sQuery(id+"F7.wireOp",EDGE,"E56"),sQuery(id+"F7.wireOp",EDGE,"E57"),sQuery(id+"F7.wireOp",EDGE,"E58"),sQuery(id+"F7.wireOp",EDGE,"E59"),sQuery(id+"F7.wireOp",EDGE,"E61"),sQuery(id+"F7.wireOp",EDGE,"E64"),sQuery(id+"F7.wireOp",EDGE,"E65")])],"isStart":true});
            cPlane(context, id + "F19", {"entities" : qUnion([Q0]), "cplaneType" : CPlaneType.OFFSET, "offset" : 300 * mm, "width" : 150 * mm, "height" : 150 * mm});
        }
        {
            var Q0;
            Q0=makeQuery(id+"F1.opExtrude","SWEPT_BODY",BODY,{"disambiguationData":[OSD([sQuery(id+"F0.wireOp",EDGE,"E0"),sQuery(id+"F0.wireOp",EDGE,"E1"),sQuery(id+"F0.wireOp",EDGE,"E2"),sQuery(id+"F0.wireOp",EDGE,"E3"),sQuery(id+"F0.wireOp",EDGE,"E5"),sQuery(id+"F0.wireOp",EDGE,"E6")])]});
            var Q1;
            Q1=makeQuery(id+"F18.opPattern","COPY",BODY,{"derivedFrom":makeQuery(id+"F15.opExtrude","SWEPT_BODY",BODY,{"disambiguationData":[OSD([sQuery(id+"F14.wireOp",EDGE,"E116"),sQuery(id+"F14.wireOp",EDGE,"E117"),sQuery(id+"F14.wireOp",EDGE,"E118"),sQuery(id+"F14.wireOp",EDGE,"E119"),sQuery(id+"F14.wireOp",EDGE,"E125"),sQuery(id+"F14.wireOp",EDGE,"E126"),sQuery(id+"F14.wireOp",EDGE,"E127")])]}),"instanceName":"1"});
            var Q2;
            Q2=makeQuery(id+"F8.opExtrude","SWEPT_BODY",BODY,{"disambiguationData":[OSD([sQuery(id+"F7.wireOp",EDGE,"E56"),sQuery(id+"F7.wireOp",EDGE,"E57"),sQuery(id+"F7.wireOp",EDGE,"E58"),sQuery(id+"F7.wireOp",EDGE,"E59"),sQuery(id+"F7.wireOp",EDGE,"E61"),sQuery(id+"F7.wireOp",EDGE,"E64"),sQuery(id+"F7.wireOp",EDGE,"E65"),sQuery(id+"F7.wireOp",EDGE,"a3dc1NE5-J77q-sxHU-Vcka-XX6ci5muAKLQ")])]});
            var Q3;
            Q3=makeQuery(id+"F13.opPattern","COPY",BODY,{"derivedFrom":makeQuery(id+"F1.opExtrude","SWEPT_BODY",BODY,{"disambiguationData":[OSD([sQuery(id+"F0.wireOp",EDGE,"E0"),sQuery(id+"F0.wireOp",EDGE,"E1"),sQuery(id+"F0.wireOp",EDGE,"E2"),sQuery(id+"F0.wireOp",EDGE,"E3"),sQuery(id+"F0.wireOp",EDGE,"E5"),sQuery(id+"F0.wireOp",EDGE,"E6")])]}),"instanceName":"1"});
            var Q4;
            Q4=makeQuery(id+"F15.opExtrude","SWEPT_BODY",BODY,{"disambiguationData":[OSD([sQuery(id+"F14.wireOp",EDGE,"E112"),sQuery(id+"F14.wireOp",EDGE,"E113"),sQuery(id+"F14.wireOp",EDGE,"E114"),sQuery(id+"F14.wireOp",EDGE,"E115"),sQuery(id+"F14.wireOp",EDGE,"E124"),sQuery(id+"F14.wireOp",EDGE,"E128"),sQuery(id+"F14.wireOp",EDGE,"E129")])]});
            var Q5;
            Q5=makeQuery(id+"F15.opExtrude","SWEPT_BODY",BODY,{"disambiguationData":[OSD([sQuery(id+"F14.wireOp",EDGE,"E116"),sQuery(id+"F14.wireOp",EDGE,"E117"),sQuery(id+"F14.wireOp",EDGE,"E118"),sQuery(id+"F14.wireOp",EDGE,"E119"),sQuery(id+"F14.wireOp",EDGE,"E125"),sQuery(id+"F14.wireOp",EDGE,"E126"),sQuery(id+"F14.wireOp",EDGE,"E127")])]});
            var Q6;
            Q6=makeQuery(id+"F18.opPattern","COPY",BODY,{"derivedFrom":makeQuery(id+"F15.opExtrude","SWEPT_BODY",BODY,{"disambiguationData":[OSD([sQuery(id+"F14.wireOp",EDGE,"E112"),sQuery(id+"F14.wireOp",EDGE,"E113"),sQuery(id+"F14.wireOp",EDGE,"E114"),sQuery(id+"F14.wireOp",EDGE,"E115"),sQuery(id+"F14.wireOp",EDGE,"E124"),sQuery(id+"F14.wireOp",EDGE,"E128"),sQuery(id+"F14.wireOp",EDGE,"E129")])]}),"instanceName":"1"});
            var Q7;
            Q7=makeQuery(id+"FXQwG3oA6umNqDY_4.opExtrude","SWEPT_BODY",BODY,{"disambiguationData":[OSD([sQuery(id+"FCqva40XrJ4V126_4.wireOp",EDGE,"78n3ciA1-uomn-yBy7-r25V-WP5mjnDSE51b"),sQuery(id+"FCqva40XrJ4V126_4.wireOp",EDGE,"Y7wIcyIb-FoVn-5xuj-phSf-5b2q6NPwGIWa"),sQuery(id+"FCqva40XrJ4V126_4.wireOp",EDGE,"lD3lK019-n7aM-jMCI-HHF9-xqF3XS0OYAXL"),sQuery(id+"FCqva40XrJ4V126_4.wireOp",EDGE,"R12ONif3-EaFE-nE2H-PnFe-9cwd8XNfsR2q"),sQuery(id+"FCqva40XrJ4V126_4.wireOp",EDGE,"ELFCeRas-l5d1-hcGD-FCQb-yX8VnA3mtWFh"),sQuery(id+"FCqva40XrJ4V126_4.wireOp",EDGE,"DLMsOrrG-DfZs-aLlZ-V3jN-I2WMqElGk50g"),sQuery(id+"FCqva40XrJ4V126_4.wireOp",EDGE,"UV9GXJqr-dj6A-OMwq-xkIZ-CN148UZTotel")])]});
            var Q8;
            Q8=qCreatedBy(id+"F19.planeOp",FACE);
            mirror(context, id + "F20", {"entities" : qUnion([Q0, Q1, Q2, Q3, Q4, Q5, Q6, Q7]), "mirrorPlane" : qUnion([Q8])});
        }
        {
            var Q0;
            Q0=qCreatedBy(id+"F19.planeOp",FACE);
            var sketch = newSketch(context, id + "F21", { "sketchPlane" : qUnion([Q0])});
            skCircle(sketch, "E130", {"center": v(-392.9, 1025) * mm, "radius": 5.9 * mm});
            skSolve(sketch);
        }
        {
            var Q0;
            Q0 = qSketchRegion(id + "F21", true);
            extrude(context, id + "F22", {"entities" : qUnion([Q0]), "endBound" : BoundingType.SYMMETRIC, "depth" : 760 * mm, "offsetDistance" : 25 * mm});
        }
        {
            var Q0;
            Q0=qCreatedBy(id+"F19.planeOp",FACE);
            var sketch = newSketch(context, id + "F23", { "sketchPlane" : qUnion([Q0])});
            skCircle(sketch, "E131", {"center": v(-392.9, 1025) * mm, "radius": 30 * mm});
            skCircle(sketch, "E132", {"center": v(-392.9, 1025) * mm, "radius": 6.25 * mm});
            skSolve(sketch);
        }
        {
            var Q0;
            Q0 = qSketchRegion(id + "F23", true);
            extrude(context, id + "F24", {"entities" : qUnion([Q0]), "endBound" : BoundingType.SYMMETRIC, "depth" : 590 * mm, "offsetDistance" : 25 * mm});
        }
        {
            var Q0;
            Q0=makeQuery(id+"F22.opExtrude","CAP_EDGE",EDGE,{"disambiguationData":[OSD([sQuery(id+"F21.wireOp",EDGE,"E130")])],"isStart":true});
            var Q1;
            Q1=makeQuery(id+"F22.opExtrude","CAP_EDGE",EDGE,{"disambiguationData":[OSD([sQuery(id+"F21.wireOp",EDGE,"E130")])],"isStart":false});
            chamfer(context, id + "F25", {"entities" : qUnion([Q0, Q1]), "width" : 2 * mm, "tangentPropagation" : true});
        }
        {
            var Q0;
            Q0=makeQuery(id+"F24.opExtrude","CAP_EDGE",EDGE,{"disambiguationData":[OSD([sQuery(id+"F23.wireOp",EDGE,"E131")])],"isStart":false});
            var Q1;
            Q1=makeQuery(id+"F24.opExtrude","CAP_EDGE",EDGE,{"disambiguationData":[OSD([sQuery(id+"F23.wireOp",EDGE,"E131")])],"isStart":true});
            chamfer(context, id + "F26", {"entities" : qUnion([Q0, Q1]), "width" : 5 * mm, "tangentPropagation" : true});
        }
        {
            var Q0;
            Q0=makeQuery(id+"F24.opExtrude","SWEPT_FACE",FACE,{"disambiguationData":[OSD([sQuery(id+"F23.wireOp",EDGE,"E131")])]});
            cPlane(context, id + "F27", {"entities" : qUnion([Q0]), "cplaneType" : CPlaneType.LINE_ANGLE, "offset" : 25 * mm, "angle" : 0 * degree, "width" : 150 * mm, "height" : 150 * mm});
        }
        {
            var Q0;
            {var subQ0=sQuery(id+"F0.wireOp",EDGE,"E0");Q0=makeQuery(id+"F4.boolean.opBoolean","SPLIT",FACE,{"disambiguationData":[TD([makeQuery(id+"F4.opExtrude","SWEPT_FACE",FACE,{"disambiguationData":[OSD([sQuery(id+"F3.wireOp",EDGE,"E20.MirrorCS")])]})])],"derivedFrom":makeQuery(id+"F1.opExtrude","SWEPT_FACE",FACE,{"disambiguationData":[OSD([subQ0])]})});}
            var sketch = newSketch(context, id + "F28", { "sketchPlane" : qUnion([Q0])});
            skLineSegment(sketch, "E133", {"start": v(0, 225) * mm, "end": v(0, 175) * mm});
            skLineSegment(sketch, "E134", {"start": v(-720, 175) * mm, "end": v(0, 175) * mm});
            skLineSegment(sketch, "E135", {"start": v(-720, 175) * mm, "end": v(-720, 225) * mm});
            skLineSegment(sketch, "E136", {"start": v(0, 225) * mm, "end": v(-720, 225) * mm});
            skLineSegment(sketch, "E137", {"start": v(-720, 200) * mm, "end": v(0, 200) * mm, "construction": true});
            skCircle(sketch, "E138", {"center": v(-30, 200) * mm, "radius": 6.25 * mm});
            skCircle(sketch, "E139", {"center": v(-690, 200) * mm, "radius": 6.25 * mm});
            skSolve(sketch);
        }
        {
            var Q0;
            Q0 = qSketchRegion(id + "F28", true);
            extrude(context, id + "F29", {"entities" : qUnion([Q0]), "depth" : 4 * mm, "offsetDistance" : 25 * mm});
        }
        {
            var Q0;
            Q0=makeQuery(id+"F29.opExtrude","SWEPT_EDGE",EDGE,{"disambiguationData":[OSD([sQuery(id+"F28.wireOp",EDGE,"E133"),sQuery(id+"F28.wireOp",EDGE,"E136")])]});
            var Q1;
            Q1=makeQuery(id+"F29.opExtrude","SWEPT_EDGE",EDGE,{"disambiguationData":[OSD([sQuery(id+"F28.wireOp",EDGE,"E133"),sQuery(id+"F28.wireOp",EDGE,"E134")])]});
            var Q2;
            Q2=makeQuery(id+"F29.opExtrude","SWEPT_EDGE",EDGE,{"disambiguationData":[OSD([sQuery(id+"F28.wireOp",EDGE,"E135"),sQuery(id+"F28.wireOp",EDGE,"E136")])]});
            var Q3;
            Q3=makeQuery(id+"F29.opExtrude","SWEPT_EDGE",EDGE,{"disambiguationData":[OSD([sQuery(id+"F28.wireOp",EDGE,"E134"),sQuery(id+"F28.wireOp",EDGE,"E135")])]});
            fillet(context, id + "F30", {"entities" : qUnion([Q0, Q1, Q2, Q3]), "radius" : 7.5 * mm, "tangentPropagation" : true, "allowEdgeOverflow" : false});
        }
        {
            var Q0;
            Q0=makeQuery(id+"F29.opExtrude","SWEPT_BODY",BODY,{"disambiguationData":[OSD([sQuery(id+"F28.wireOp",EDGE,"E133"),sQuery(id+"F28.wireOp",EDGE,"E134"),sQuery(id+"F28.wireOp",EDGE,"E135"),sQuery(id+"F28.wireOp",EDGE,"E136"),sQuery(id+"F28.wireOp",EDGE,"E138"),sQuery(id+"F28.wireOp",EDGE,"E139")])]});
            var Q1;
            Q1=qCreatedBy(id+"F12.planeOp",FACE);
            mirror(context, id + "F31", {"entities" : qUnion([Q0]), "mirrorPlane" : qUnion([Q1])});
        }
    });
